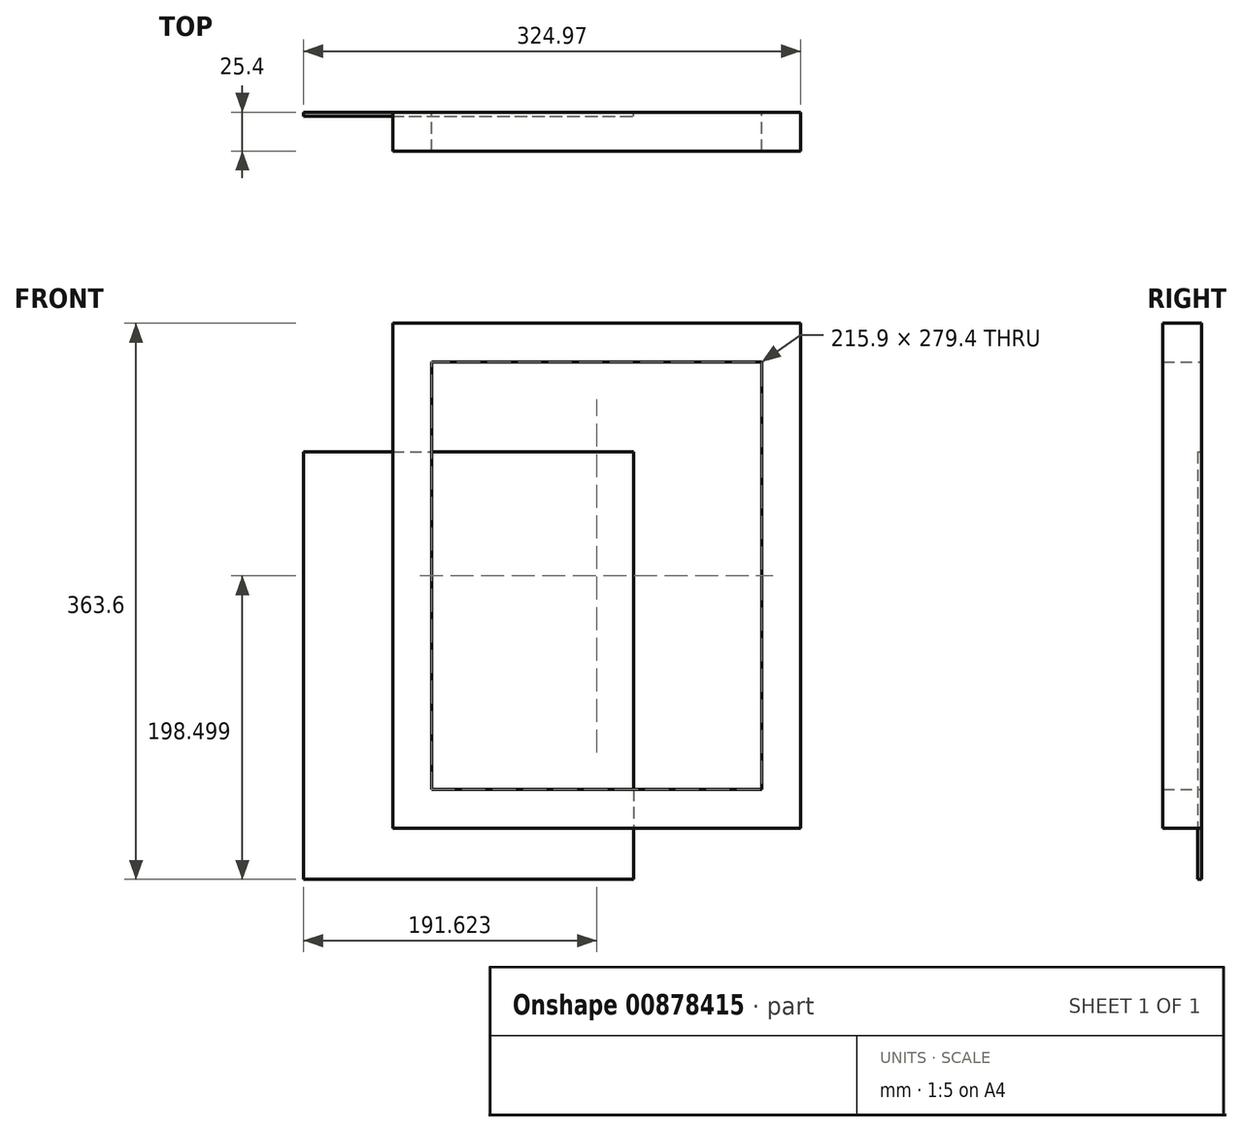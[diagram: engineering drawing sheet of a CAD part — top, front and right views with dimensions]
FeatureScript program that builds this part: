
annotation { "Feature Type Name" : "Feature", "Feature Type Description" : "" }
export const myFeature = defineFeature(function(context is Context, id is Id, definition is map)
    precondition{}
    {
        {
            var Q0;
            Q0=qCreatedBy(makeId("Front.planeOp"),FACE);
            var sketch = newSketch(context, id + "F0", { "sketchPlane" : qUnion([Q0])});
            skLineSegment(sketch, "E0.bottom", {"start": v(-29.74, 243.29) * mm, "end": v(186.16, 243.29) * mm});
            skLineSegment(sketch, "E0.top", {"start": v(-29.74, -36.11) * mm, "end": v(186.16, -36.11) * mm});
            skLineSegment(sketch, "E0.left", {"start": v(-29.74, 243.29) * mm, "end": v(-29.74, -36.11) * mm});
            skLineSegment(sketch, "E0.right", {"start": v(186.16, 243.29) * mm, "end": v(186.16, -36.11) * mm});
            skLineSegment(sketch, "E1.0", {"start": v(-55.14, 268.69) * mm, "end": v(-55.14, -61.51) * mm});
            skLineSegment(sketch, "E1.1", {"start": v(-55.14, 268.69) * mm, "end": v(211.56, 268.69) * mm});
            skLineSegment(sketch, "E1.2", {"start": v(211.56, 268.69) * mm, "end": v(211.56, -61.51) * mm});
            skLineSegment(sketch, "E1.3", {"start": v(-55.14, -61.51) * mm, "end": v(211.56, -61.51) * mm});
            skSolve(sketch);
        }
        {
            var Q0;
            Q0=makeQuery(id+"F0.imprint","IMPRINT",FACE,{"disambiguationData":[TD([[makeQuery(id+"F0.imprint","IMPRINT",EDGE,{"derivedFrom":sQuery(id+"F0.wireOp",EDGE,"E0.bottom")}),1.0]])]});
            extrude(context, id + "F1", {"entities" : qUnion([Q0]), "depth" : 25.4 * mm, "offsetDistance" : 25.4 * mm});
        }
        {
            var Q0;
            Q0=qCreatedBy(makeId("Front.planeOp"),FACE);
            var sketch = newSketch(context, id + "F2", { "sketchPlane" : qUnion([Q0])});
            skLineSegment(sketch, "E2.bottom", {"start": v(-113.41, 184.5) * mm, "end": v(102.49, 184.5) * mm});
            skLineSegment(sketch, "E2.top", {"start": v(-113.41, -94.9) * mm, "end": v(102.49, -94.9) * mm});
            skLineSegment(sketch, "E2.left", {"start": v(-113.41, 184.5) * mm, "end": v(-113.41, -94.9) * mm});
            skLineSegment(sketch, "E2.right", {"start": v(102.49, 184.5) * mm, "end": v(102.49, -94.9) * mm});
            skSolve(sketch);
        }
        {
            var Q0;
            Q0 = qSketchRegion(id + "F2", true);
            extrude(context, id + "F3", {"entities" : qUnion([Q0]), "depth" : 2.54 * mm, "offsetDistance" : 25.4 * mm});
        }
    });
